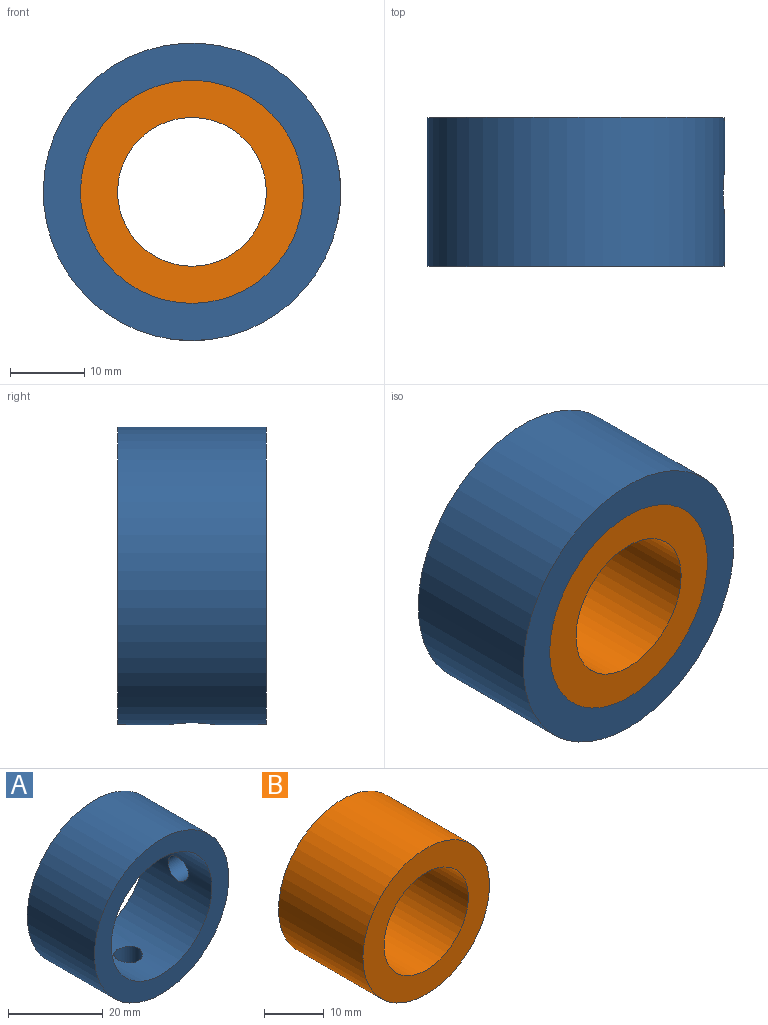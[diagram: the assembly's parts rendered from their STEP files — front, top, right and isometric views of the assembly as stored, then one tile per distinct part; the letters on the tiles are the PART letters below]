
ASSEMBLY  parts=2 mates=1
PART A: 6 faces, bbox 40x20x40 mm
  f0: cylinder r=15mm len=30mm, axis (0,1,0), area 1828.2mm2, adj f2,f3,f4,f5
  f1: cylinder r=20mm len=40mm, axis (0,1,0), area 2456.6mm2, adj f2,f3,f4,f5
  f2: plane 40x40mm, normal (0,-1,0), area 549.8mm2, adj f0,f1
  f3: plane 40x40mm, normal (0,1,0), area 549.8mm2, adj f0,f1
  f4: cylinder r=3mm len=6mm, axis (1,0,0), area 95mm2, adj f0,f1
  f5: cylinder r=3mm len=6mm, axis (0,0,1), area 95mm2, adj f0,f1
PART B: 4 faces, bbox 30x20x30 mm
  f0: cylinder r=10mm len=20mm, axis (0,1,0), area 1256.6mm2, adj f2,f3
  f1: cylinder r=15mm len=30mm, axis (0,1,0), area 1885mm2, adj f2,f3
  f2: plane 30x30mm, normal (0,-1,0), area 392.7mm2, adj f0,f1
  f3: plane 30x30mm, normal (0,1,0), area 392.7mm2, adj f0,f1
PLACE A t=(26.17,-11.05,12.87)mm
PLACE B t=(-27.11,-11.05,56.92)mm
MATE cylindrical B.f0 <-> A.f0  axis (0,1,0) through (-51.41,-11.05,12.96)mm
